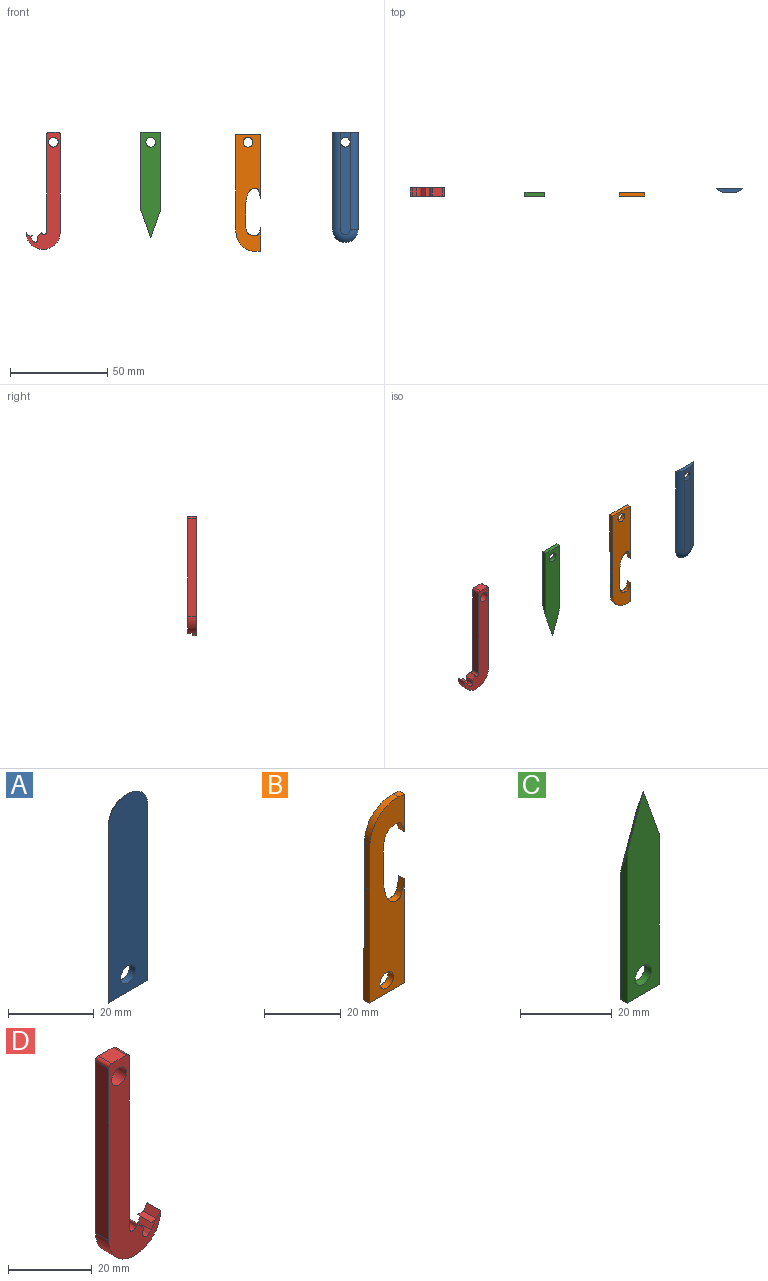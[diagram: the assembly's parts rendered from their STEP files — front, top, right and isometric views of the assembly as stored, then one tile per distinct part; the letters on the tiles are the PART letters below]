
ASSEMBLY  parts=4 mates=3
PART A: 8 faces, bbox 13x2x56.5 mm
  f0: plane 5x5mm, normal (0,1,0), area 15.2mm2, adj f1,f2,f5,f7
  f1: plane 13x2mm, normal (0,0,-1), area 21.2mm2, adj f0,f3,f5,f7
  f2: cylinder r=2.5mm len=5mm, axis (0,1,0), area 31.4mm2, adj f0,f3,f4
  f3: plane 56.5x13mm, normal (0,-1,0), area 696.7mm2, adj f1,f2,f5,f6,f7
  f4: plane 47.5x5mm, normal (0,1,0), area 225mm2, adj f2,f5,f6,f7
  f5: cylinder r=5mm len=50mm, axis (0,0,-1), area 231.8mm2, adj f0,f1,f3,f4,f6
  f6: torus R=2.5mm, axis (0,1,0), area 67.8mm2, adj f3,f4,f5,f7
  f7: cylinder r=5mm len=50mm, axis (0,0,1), area 231.8mm2, adj f0,f1,f3,f4,f6
PART B: 11 faces, bbox 13x2x60.1 mm
  f0: cylinder r=10mm len=10.63mm, axis (0,1,0), area 32.7mm2, adj f1,f8,f9,f10
  f1: plane 14.35x2mm, normal (-1,0,0), area 28.7mm2, adj f0,f2,f9,f10
  f2: plane 35.8x2mm, normal (-1,0,0.01), area 71.6mm2, adj f1,f3,f9,f10
  f3: plane 13x2mm, normal (0,0,-1), area 26mm2, adj f2,f4,f9,f10
  f4: plane 33x2mm, normal (1,0,0), area 66mm2, adj f3,f5,f9,f10
  f5: extruded ~24.53x7.8mm, area 83.5mm2, adj f4,f6,f9,f10
  f6: plane 12x2mm, normal (1,0,0), area 24mm2, adj f5,f8,f9,f10
  f7: cylinder r=2.5mm len=5mm, axis (0,1,0), area 31.4mm2, adj f9,f10
  f8: plane 2.05x2mm, normal (0.06,0,1), area 4.1mm2, adj f0,f6,f9,f10
  f9: plane 60.15x13mm, normal (0,-1,0), area 558.4mm2, adj f0,f1,f2,f3,f4,f5,f6,f7
  f10: plane 60.15x13mm, normal (0,1,0), area 558.4mm2, adj f0,f1,f2,f3,f4,f5,f6,f7
PART C: 8 faces, bbox 10x2x54.1 mm
  f0: plane 40x2mm, normal (-1,0,0), area 74mm2, adj f1,f4,f5,f7
  f1: plane 10x2mm, normal (0,0,-1), area 20mm2, adj f0,f2,f4,f5
  f2: plane 40x2mm, normal (1,0,0), area 74mm2, adj f1,f4,f5,f6
  f3: cylinder r=2.5mm len=5mm, axis (0,1,0), area 31.4mm2, adj f4,f5
  f4: plane 54.14x10mm, normal (0,-1,0), area 451.1mm2, adj f0,f1,f2,f3,f6,f7
  f5: plane 48.14x10mm, normal (0,1,0), area 391.1mm2, adj f0,f1,f2,f3,f6,f7
  f6: plane 20.14x5mm, normal (0.67,0.71,0.24), area 42.4mm2, adj f2,f4,f5,f7
  f7: plane 20.14x5mm, normal (-0.67,0.71,0.24), area 42.4mm2, adj f0,f4,f5,f6
PART D: 17 faces, bbox 17.6x4.5x60.1 mm
  f0: cylinder r=1.22mm len=4.5mm, axis (0,1,0), area 16.5mm2, adj f1,f12,f13,f16
  f1: plane 50.3x4.5mm, normal (1,0,0), area 226.4mm2, adj f0,f12,f13,f15
  f2: plane 5x4.5mm, normal (0,0,1), area 22.5mm2, adj f12,f13,f14,f15
  f3: plane 50.3x4.5mm, normal (-1,0,0), area 226.3mm2, adj f4,f12,f13,f14
  f4: cylinder r=8.76mm len=17.53mm, axis (0,1,0), area 123.9mm2, adj f3,f5,f12,f13
  f5: plane 4.5x1.71mm, normal (-0.78,0,0.62), area 9.9mm2, adj f4,f6,f12,f13
  f6: plane 4.5x1.91mm, normal (0,0,1), area 8.6mm2, adj f5,f7,f12,f13
  f7: plane 4.5x1.17mm, normal (-0.62,0,-0.78), area 6.7mm2, adj f6,f8,f12,f13
  f8: plane 4.5x1.4mm, normal (-0.78,0,0.62), area 8.1mm2, adj f7,f9,f12,f13
  f9: extruded ~4.5x3.12mm, area 26.3mm2, adj f8,f10,f12,f13
  f10: plane 4.5x2.3mm, normal (0.64,0,0.77), area 13.4mm2, adj f9,f12,f13,f16
  f11: cylinder r=2.5mm len=5mm, axis (0,1,0), area 70.7mm2, adj f12,f13
  f12: plane 60.06x17.56mm, normal (0,-1,0), area 435.9mm2, adj f0,f1,f2,f3,f4,f5,f6,f7
  f13: plane 60.06x17.56mm, normal (0,1,0), area 435.9mm2, adj f0,f1,f2,f3,f4,f5,f6,f7
  f14: cylinder r=1mm len=4.5mm, axis (0,1,0), area 7.1mm2, adj f2,f3,f12,f13
  f15: cylinder r=1mm len=4.5mm, axis (0,1,0), area 7.1mm2, adj f1,f2,f12,f13
  f16: cylinder r=0.1mm len=4.5mm, axis (0,1,0), area 0.9mm2, adj f0,f10,f12,f13
PLACE A rot(axis=(1,0,0),180deg) t=(70.98,-21.39,-78.96)mm
PLACE B rot(axis=(1,0,0),180deg) t=(43.87,-23.39,-94.27)mm
PLACE C rot(axis=(0,1,0),180deg) t=(-55.39,-21.39,-44.64)mm
PLACE D rot(axis=(0,0,1),180deg) t=(-125.18,-23.39,-63.82)mm
MATE fastened A.f2 <-> C.f5  axis (0,-1,0) through (55.2,-21.39,-42.23)mm
MATE fastened B.f7 <-> C.f4  axis (0,-1,0) through (5.2,-23.39,-42.23)mm
MATE fastened D.f11 <-> C.f4  axis (0,-1,0) through (-94.8,-23.39,-42.23)mm
